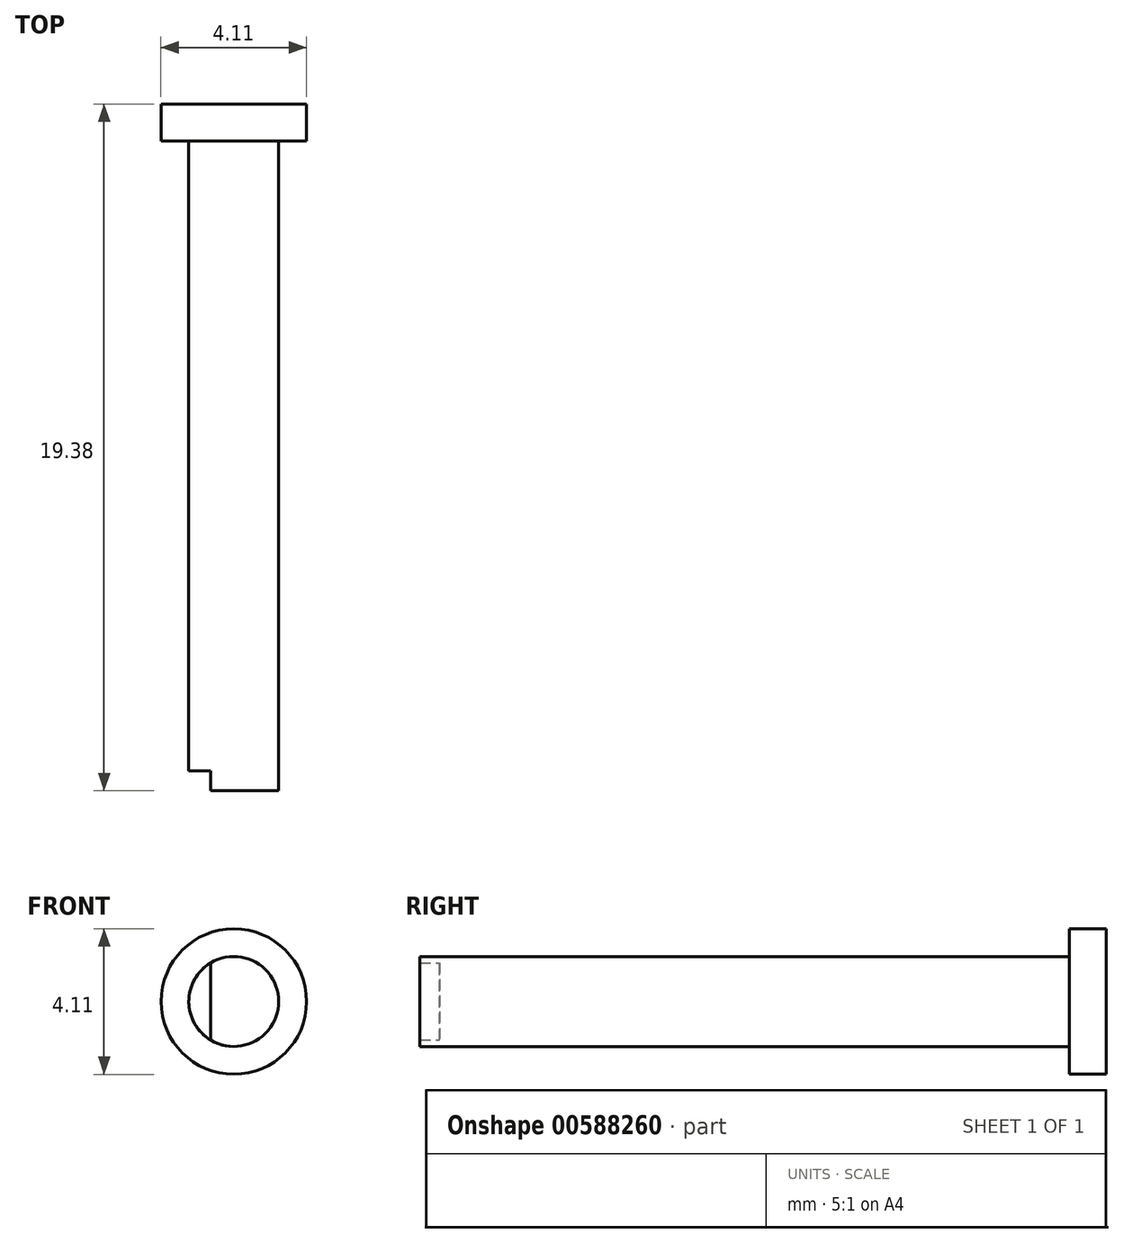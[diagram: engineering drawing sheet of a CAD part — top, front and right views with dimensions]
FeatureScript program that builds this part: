
annotation { "Feature Type Name" : "Feature", "Feature Type Description" : "" }
export const myFeature = defineFeature(function(context is Context, id is Id, definition is map)
    precondition{}
    {
        {
            var Q0;
            Q0=qCreatedBy(makeId("Front.planeOp"),FACE);
            var sketch = newSketch(context, id + "F0", { "sketchPlane" : qUnion([Q0])});
            skCircle(sketch, "E0", {"center": v(-44.91, 42.52) * mm, "radius": 1.27 * mm});
            skSolve(sketch);
        }
        {
            var Q0;
            Q0=makeQuery(id+"F0.imprint","IMPRINT",FACE,{"disambiguationData":[TD([[makeQuery(id+"F0.imprint","IMPRINT",EDGE,{"derivedFrom":sQuery(id+"F0.wireOp",EDGE,"E0")}),1.0]])]});
            extrude(context, id + "F1", {"entities" : qUnion([Q0]), "depth" : 17.78 * mm, "offsetDistance" : 25.4 * mm});
        }
        {
            var Q0;
            Q0=makeQuery(id+"F1.opExtrude","CAP_FACE",FACE,{"disambiguationData":[OSD([sQuery(id+"F0.wireOp",EDGE,"E0")])],"isStart":true});
            var sketch = newSketch(context, id + "F2", { "sketchPlane" : qUnion([Q0])});
            skLineSegment(sketch, "E1", {"start": v(44.28, 42.52) * mm, "end": v(44.28, 43.62) * mm});
            skLineSegment(sketch, "E2", {"start": v(44.28, 43.62) * mm, "end": v(44.28, 41.42) * mm});
            skLineSegment(sketch, "E3", {"start": v(45.55, 41.42) * mm, "end": v(45.55, 43.62) * mm});
            skLineSegment(sketch, "E4", {"start": v(45.55, 43.62) * mm, "end": v(44.28, 43.62) * mm});
            skLineSegment(sketch, "E5", {"start": v(44.28, 41.42) * mm, "end": v(45.55, 41.42) * mm});
            skCircle(sketch, "E6", {"center": v(44.91, 42.52) * mm, "radius": 2.05 * mm});
            skPoint(sketch, "E6.centerSnap0", {"position": v(44.91, 43.62) * mm});
            skSolve(sketch);
        }
        {
            var Q0;
            Q0=makeQuery(id+"F2.imprint","IMPRINT",FACE,{"disambiguationData":[TD([[makeQuery(id+"F2.imprint","IMPRINT",EDGE,{"derivedFrom":sQuery(id+"F2.wireOp",EDGE,"E6")}),1.0]])]});
            var Q1;
            {var subQ0=sQuery(id+"F2.wireOp",EDGE,"E2");var subQ3=makeQuery(id+"F2.imprint","IMPRINT",VERTEX,{"derivedFrom":subQ0});Q1=makeQuery(id+"F2.imprint","IMPRINT",FACE,{"disambiguationData":[TD([[makeQuery(id+"F2.imprint","IMPRINT",EDGE,{"disambiguationData":[TD([[subQ3,1.0]])],"derivedFrom":subQ0}),-1.0]])]});}
            var Q2;
            Q2=makeQuery(id+"F2.imprint","IMPRINT",FACE,{"disambiguationData":[TD([[makeQuery(id+"F2.imprint","IMPRINT",EDGE,{"derivedFrom":sQuery(id+"F2.wireOp",EDGE,"E3")}),1.0]])]});
            var Q3;
            {var subQ0=sQuery(id+"F2.wireOp",EDGE,"E4");Q3=makeQuery(id+"F2.imprint","IMPRINT",FACE,{"disambiguationData":[TD([[makeQuery(id+"F2.imprint","IMPRINT",EDGE,{"derivedFrom":subQ0}),-1.0]])]});}
            var Q4;
            {var subQ0=sQuery(id+"F2.wireOp",EDGE,"E3");Q4=makeQuery(id+"F2.imprint","IMPRINT",FACE,{"disambiguationData":[TD([[makeQuery(id+"F2.imprint","IMPRINT",EDGE,{"derivedFrom":subQ0}),-1.0]])]});}
            extrude(context, id + "F3", {"entities" : qUnion([Q0, Q1, Q2, Q3, Q4]), "operationType" : NewBodyOperationType.ADD, "depth" : 1.04 * mm, "offsetDistance" : 25.4 * mm});
        }
        {
            var Q0;
            Q0=makeQuery(id+"F1.opExtrude","CAP_FACE",FACE,{"disambiguationData":[OSD([sQuery(id+"F0.wireOp",EDGE,"E0")])],"isStart":false});
            var sketch = newSketch(context, id + "F4", { "sketchPlane" : qUnion([Q0])});
            skLineSegment(sketch, "E7", {"start": v(-45.57, 42.52) * mm, "end": v(-45.57, 41.43) * mm});
            skLineSegment(sketch, "E8", {"start": v(-45.57, 41.43) * mm, "end": v(-45.57, 43.6) * mm});
            skArc(sketch, "E9", {"start": v(-45.57, 41.43) * mm, "mid": v(-43.64, 42.52) * mm, "end": v(-45.57, 43.6) * mm});
            skSolve(sketch);
        }
        {
            var Q0;
            {var subQ0=sQuery(id+"F4.wireOp",EDGE,"E9");Q0=makeQuery(id+"F4.imprint","IMPRINT",FACE,{"disambiguationData":[TD([[makeQuery(id+"F4.imprint","IMPRINT",EDGE,{"derivedFrom":subQ0}),1.0]])]});}
            extrude(context, id + "F5", {"entities" : qUnion([Q0]), "operationType" : NewBodyOperationType.ADD, "depth" : 0.56 * mm, "offsetDistance" : 25.4 * mm});
        }
    });
